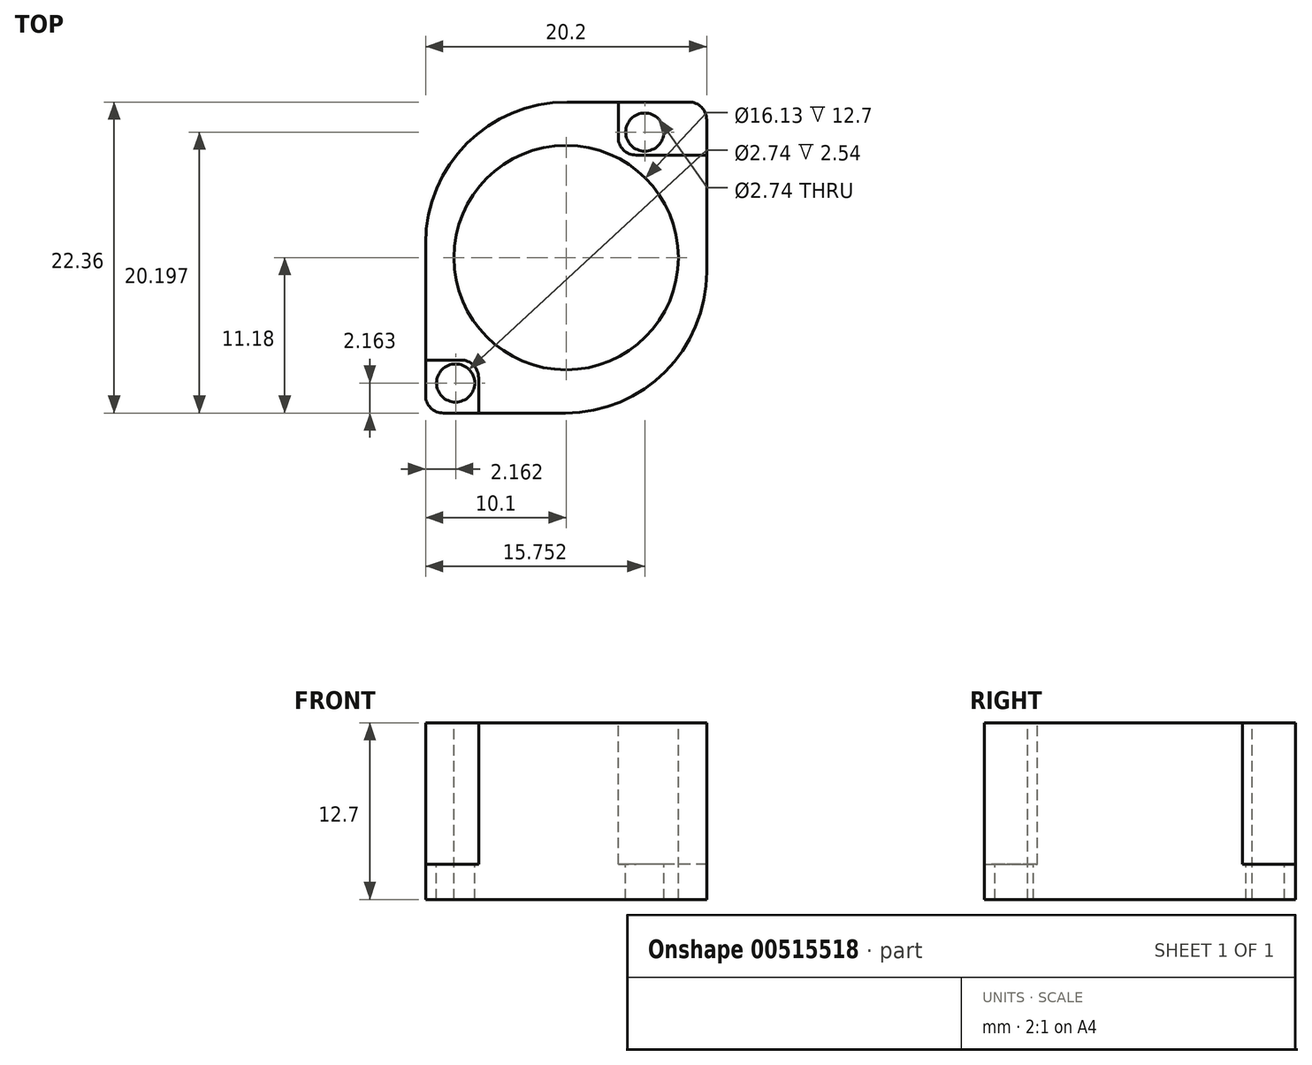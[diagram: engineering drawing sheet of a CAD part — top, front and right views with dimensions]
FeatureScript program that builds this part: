
annotation { "Feature Type Name" : "Feature", "Feature Type Description" : "" }
export const myFeature = defineFeature(function(context is Context, id is Id, definition is map)
    precondition{}
    {
        {
            var Q0;
            Q0=qCreatedBy(makeId("Top.planeOp"),FACE);
            var sketch = newSketch(context, id + "F0", { "sketchPlane" : qUnion([Q0])});
            skLineSegment(sketch, "E0.bottom", {"start": v(10.1, 11.18) * mm, "end": v(-10.1, 11.18) * mm});
            skLineSegment(sketch, "E0.top", {"start": v(10.1, -11.18) * mm, "end": v(-10.1, -11.18) * mm});
            skLineSegment(sketch, "E0.left", {"start": v(10.1, 11.18) * mm, "end": v(10.1, -11.18) * mm});
            skLineSegment(sketch, "E0.right", {"start": v(-10.1, 11.18) * mm, "end": v(-10.1, -11.18) * mm});
            skPoint(sketch, "E0.middle", {"position": v(0, 0) * mm});
            skSolve(sketch);
        }
        {
            var Q0;
            Q0=makeQuery(id+"F0.imprint","IMPRINT",FACE,{"disambiguationData":[TD([[makeQuery(id+"F0.imprint","IMPRINT",EDGE,{"derivedFrom":sQuery(id+"F0.wireOp",EDGE,"E0.bottom")}),1.0]])]});
            extrude(context, id + "F1", {"entities" : qUnion([Q0]), "depth" : 12.7 * mm, "offsetDistance" : 25.4 * mm});
        }
        {
            var Q0;
            Q0=makeQuery(id+"F1.opExtrude","CAP_FACE",FACE,{"disambiguationData":[OSD([sQuery(id+"F0.wireOp",EDGE,"E0.bottom"),sQuery(id+"F0.wireOp",EDGE,"E0.top"),sQuery(id+"F0.wireOp",EDGE,"E0.left"),sQuery(id+"F0.wireOp",EDGE,"E0.right")])],"isStart":false});
            var sketch = newSketch(context, id + "F2", { "sketchPlane" : qUnion([Q0])});
            skCircle(sketch, "E1", {"center": v(0, 0) * mm, "radius": 8.06 * mm});
            skSolve(sketch);
        }
        {
            var Q0;
            Q0=makeQuery(id+"F2.imprint","IMPRINT",FACE,{"disambiguationData":[TD([[makeQuery(id+"F2.imprint","IMPRINT",EDGE,{"derivedFrom":sQuery(id+"F2.wireOp",EDGE,"E1")}),1.0]])]});
            extrude(context, id + "F3", {"entities" : qUnion([Q0]), "operationType" : NewBodyOperationType.REMOVE, "oppositeDirection" : true, "depth" : 12.7 * mm, "offsetDistance" : 25.4 * mm});
        }
        {
            var Q0;
            Q0=makeQuery(id+"F1.opExtrude","CAP_FACE",FACE,{"disambiguationData":[OSD([sQuery(id+"F0.wireOp",EDGE,"E0.bottom"),sQuery(id+"F0.wireOp",EDGE,"E0.top"),sQuery(id+"F0.wireOp",EDGE,"E0.left"),sQuery(id+"F0.wireOp",EDGE,"E0.right")])],"isStart":false});
            var sketch = newSketch(context, id + "F4", { "sketchPlane" : qUnion([Q0])});
            skLineSegment(sketch, "E2.bottom", {"start": v(10.1, 11.18) * mm, "end": v(3.75, 11.18) * mm});
            skLineSegment(sketch, "E2.top", {"start": v(10.1, 7.37) * mm, "end": v(3.75, 7.37) * mm});
            skLineSegment(sketch, "E2.left", {"start": v(10.1, 11.18) * mm, "end": v(10.1, 7.37) * mm});
            skLineSegment(sketch, "E2.right", {"start": v(3.75, 11.18) * mm, "end": v(3.75, 7.37) * mm});
            skSolve(sketch);
        }
        {
            var Q0;
            {var subQ4=sQuery(id+"F4.wireOp",EDGE,"E2.top");Q0=makeQuery(id+"F4.imprint","IMPRINT",FACE,{"disambiguationData":[TD([[makeQuery(id+"F4.imprint","IMPRINT",EDGE,{"derivedFrom":subQ4}),1.0]])]});}
            var sketch = newSketch(context, id + "F5", { "sketchPlane" : qUnion([Q0])});
            skLineSegment(sketch, "E3.bottom", {"start": v(-10.1, -11.18) * mm, "end": v(-6.29, -11.18) * mm});
            skLineSegment(sketch, "E3.top", {"start": v(-10.1, -7.37) * mm, "end": v(-6.29, -7.37) * mm});
            skLineSegment(sketch, "E3.left", {"start": v(-10.1, -11.18) * mm, "end": v(-10.1, -7.37) * mm});
            skLineSegment(sketch, "E3.right", {"start": v(-6.29, -11.18) * mm, "end": v(-6.29, -7.37) * mm});
            skSolve(sketch);
        }
        {
            var Q0;
            Q0=makeQuery(id+"F5.imprint","IMPRINT",FACE,{"disambiguationData":[TD([[makeQuery(id+"F5.imprint","IMPRINT",EDGE,{"derivedFrom":sQuery(id+"F5.wireOp",EDGE,"E3.bottom")}),-1.0]])]});
            extrude(context, id + "F6", {"entities" : qUnion([Q0]), "operationType" : NewBodyOperationType.REMOVE, "oppositeDirection" : true, "depth" : 10.16 * mm, "offsetDistance" : 25.4 * mm});
        }
        {
            var Q0;
            Q0=makeQuery(id+"F4.imprint","IMPRINT",FACE,{"disambiguationData":[TD([[makeQuery(id+"F4.imprint","IMPRINT",EDGE,{"derivedFrom":sQuery(id+"F4.wireOp",EDGE,"E2.bottom")}),1.0]])]});
            extrude(context, id + "F7", {"entities" : qUnion([Q0]), "operationType" : NewBodyOperationType.REMOVE, "oppositeDirection" : true, "depth" : 10.16 * mm, "offsetDistance" : 25.4 * mm});
        }
        {
            var Q0;
            Q0=makeQuery(id+"F1.opExtrude","SWEPT_EDGE",EDGE,{"disambiguationData":[OSD([sQuery(id+"F0.wireOp",EDGE,"E0.bottom"),sQuery(id+"F0.wireOp",EDGE,"E0.right")])]});
            var Q1;
            Q1=makeQuery(id+"F1.opExtrude","SWEPT_EDGE",EDGE,{"disambiguationData":[OSD([sQuery(id+"F0.wireOp",EDGE,"E0.top"),sQuery(id+"F0.wireOp",EDGE,"E0.left")])]});
            fillet(context, id + "F8", {"entities" : qUnion([Q0, Q1]), "radius" : 10.16 * mm, "tangentPropagation" : true, "allowEdgeOverflow" : false});
        }
        {
            var Q0;
            Q0=makeQuery(id+"F6.boolean.opBoolean","COPY",EDGE,{"derivedFrom":makeQuery(id+"F6.opExtrude","SWEPT_EDGE",EDGE,{"disambiguationData":[OSD([sQuery(id+"F0.wireOp",EDGE,"E0.right"),sQuery(id+"F5.wireOp",EDGE,"E3.top"),sQuery(id+"F5.wireOp",EDGE,"E3.left")])]})});
            var Q1;
            Q1=makeQuery(id+"F6.boolean.opBoolean","COPY",EDGE,{"derivedFrom":makeQuery(id+"F6.opExtrude","SWEPT_EDGE",EDGE,{"disambiguationData":[OSD([sQuery(id+"F0.wireOp",EDGE,"E0.top"),sQuery(id+"F5.wireOp",EDGE,"E3.bottom"),sQuery(id+"F5.wireOp",EDGE,"E3.right")])]})});
            var Q2;
            Q2=makeQuery(id+"F7.boolean.opBoolean","COPY",EDGE,{"derivedFrom":makeQuery(id+"F7.opExtrude","SWEPT_EDGE",EDGE,{"disambiguationData":[OSD([sQuery(id+"F0.wireOp",EDGE,"E0.bottom"),sQuery(id+"F4.wireOp",EDGE,"E2.bottom"),sQuery(id+"F4.wireOp",EDGE,"E2.right")])]})});
            var Q3;
            Q3=makeQuery(id+"F7.boolean.opBoolean","COPY",EDGE,{"derivedFrom":makeQuery(id+"F7.opExtrude","SWEPT_EDGE",EDGE,{"disambiguationData":[OSD([sQuery(id+"F0.wireOp",EDGE,"E0.left"),sQuery(id+"F4.wireOp",EDGE,"E2.top"),sQuery(id+"F4.wireOp",EDGE,"E2.left")])]})});
            var Q4;
            Q4=makeQuery(id+"F7.boolean.opBoolean","COPY",EDGE,{"derivedFrom":makeQuery(id+"F7.opExtrude","SWEPT_EDGE",EDGE,{"disambiguationData":[OSD([sQuery(id+"F4.wireOp",EDGE,"E2.top"),sQuery(id+"F4.wireOp",EDGE,"E2.right")])]})});
            var Q5;
            Q5=makeQuery(id+"F6.boolean.opBoolean","COPY",EDGE,{"derivedFrom":makeQuery(id+"F6.opExtrude","SWEPT_EDGE",EDGE,{"disambiguationData":[OSD([sQuery(id+"F5.wireOp",EDGE,"E3.top"),sQuery(id+"F5.wireOp",EDGE,"E3.right")])]})});
            var Q6;
            Q6=makeQuery(id+"F1.opExtrude","SWEPT_EDGE",EDGE,{"disambiguationData":[OSD([sQuery(id+"F0.wireOp",EDGE,"E0.top"),sQuery(id+"F0.wireOp",EDGE,"E0.right")])]});
            var Q7;
            Q7=makeQuery(id+"F1.opExtrude","SWEPT_EDGE",EDGE,{"disambiguationData":[OSD([sQuery(id+"F0.wireOp",EDGE,"E0.bottom"),sQuery(id+"F0.wireOp",EDGE,"E0.left")])]});
            fillet(context, id + "F9", {"entities" : qUnion([Q0, Q1, Q2, Q3, Q4, Q5, Q6, Q7]), "radius" : 1.27 * mm, "tangentPropagation" : true, "allowEdgeOverflow" : false});
        }
        {
            var Q0;
            Q0=makeQuery(id+"F7.boolean.opBoolean","COPY",FACE,{"derivedFrom":makeQuery(id+"F7.opExtrude","CAP_FACE",FACE,{"disambiguationData":[OSD([sQuery(id+"F4.wireOp",EDGE,"E2.bottom"),sQuery(id+"F4.wireOp",EDGE,"E2.top"),sQuery(id+"F4.wireOp",EDGE,"E2.left"),sQuery(id+"F4.wireOp",EDGE,"E2.right")])],"isStart":false})});
            var sketch = newSketch(context, id + "F10", { "sketchPlane" : qUnion([Q0])});
            skCircle(sketch, "E4", {"center": v(5.65, 9.02) * mm, "radius": 1.37 * mm});
            skSolve(sketch);
        }
        {
            var Q0;
            Q0=makeQuery(id+"F6.boolean.opBoolean","COPY",FACE,{"derivedFrom":makeQuery(id+"F6.opExtrude","CAP_FACE",FACE,{"disambiguationData":[OSD([sQuery(id+"F5.wireOp",EDGE,"E3.bottom"),sQuery(id+"F5.wireOp",EDGE,"E3.top"),sQuery(id+"F5.wireOp",EDGE,"E3.left"),sQuery(id+"F5.wireOp",EDGE,"E3.right")])],"isStart":false})});
            var sketch = newSketch(context, id + "F11", { "sketchPlane" : qUnion([Q0])});
            skCircle(sketch, "E5", {"center": v(-7.94, -9.02) * mm, "radius": 1.37 * mm});
            skSolve(sketch);
        }
        {
            var Q0;
            Q0=makeQuery(id+"F11.imprint","IMPRINT",FACE,{"disambiguationData":[TD([[makeQuery(id+"F11.imprint","IMPRINT",EDGE,{"derivedFrom":sQuery(id+"F11.wireOp",EDGE,"E5")}),1.0]])]});
            extrude(context, id + "F12", {"entities" : qUnion([Q0]), "operationType" : NewBodyOperationType.REMOVE, "oppositeDirection" : true, "depth" : 2.54 * mm, "offsetDistance" : 25.4 * mm});
        }
        {
            var Q0;
            Q0=makeQuery(id+"F10.imprint","IMPRINT",FACE,{"disambiguationData":[TD([[makeQuery(id+"F10.imprint","IMPRINT",EDGE,{"derivedFrom":sQuery(id+"F10.wireOp",EDGE,"E4")}),1.0]])]});
            extrude(context, id + "F13", {"entities" : qUnion([Q0]), "operationType" : NewBodyOperationType.REMOVE, "oppositeDirection" : true, "depth" : 2.54 * mm, "offsetDistance" : 25.4 * mm});
        }
    });
